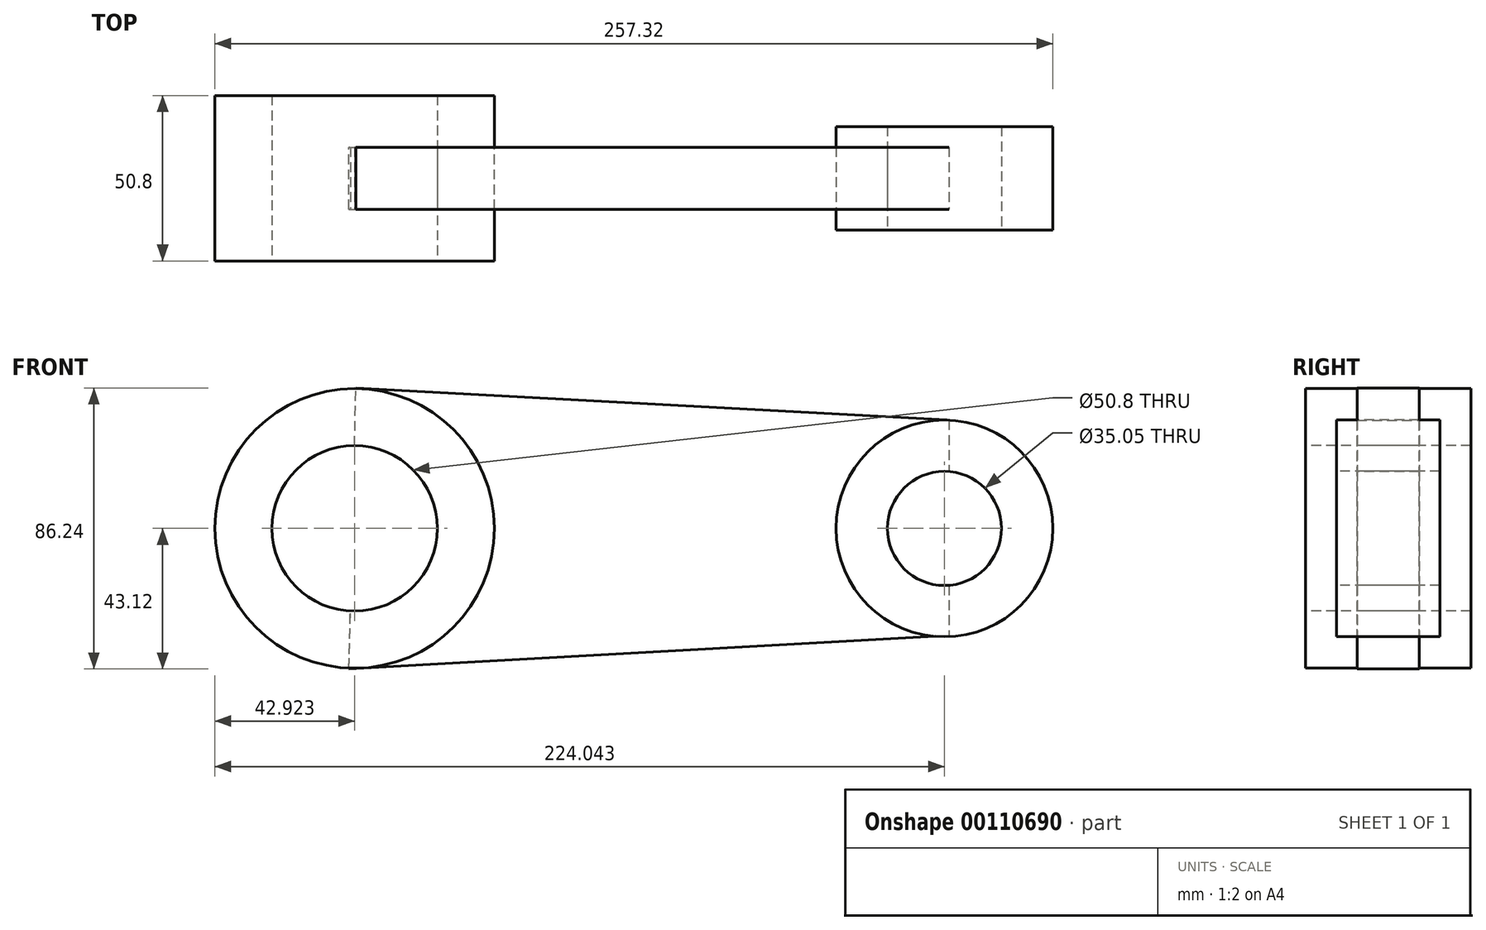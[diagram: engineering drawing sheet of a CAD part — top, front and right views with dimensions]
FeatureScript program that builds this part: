
annotation { "Feature Type Name" : "Feature", "Feature Type Description" : "" }
export const myFeature = defineFeature(function(context is Context, id is Id, definition is map)
    precondition{}
    {
        {
            var Q0;
            Q0=qCreatedBy(makeId("Front.planeOp"),FACE);
            var sketch = newSketch(context, id + "F0", { "sketchPlane" : qUnion([Q0])});
            skCircle(sketch, "E0", {"center": v(-91.09, 0) * mm, "radius": 42.93 * mm});
            skSolve(sketch);
        }
        {
            var Q0;
            Q0=qCreatedBy(makeId("Front.planeOp"),FACE);
            var sketch = newSketch(context, id + "F1", { "sketchPlane" : qUnion([Q0])});
            skCircle(sketch, "E1", {"center": v(90.03, 0) * mm, "radius": 33.27 * mm});
            skSolve(sketch);
        }
        {
            var Q0;
            Q0=makeQuery(id+"F0.imprint","IMPRINT",FACE,{"disambiguationData":[TD([[makeQuery(id+"F0.imprint","IMPRINT",EDGE,{"derivedFrom":sQuery(id+"F0.wireOp",EDGE,"E0")}),1.0]])]});
            extrude(context, id + "F2", {"entities" : qUnion([Q0]), "depth" : 25.4 * mm, "hasSecondDirection" : true, "secondDirectionOppositeDirection" : true, "secondDirectionDepth" : 25.4 * mm});
        }
        {
            var Q0;
            Q0=makeQuery(id+"F1.imprint","IMPRINT",FACE,{"disambiguationData":[TD([[makeQuery(id+"F1.imprint","IMPRINT",EDGE,{"derivedFrom":sQuery(id+"F1.wireOp",EDGE,"E1")}),1.0]])]});
            extrude(context, id + "F3", {"entities" : qUnion([Q0]), "oppositeDirection" : true, "depth" : 15.88 * mm, "hasSecondDirection" : true, "secondDirectionOppositeDirection" : false, "secondDirectionDepth" : 15.88 * mm});
        }
        {
            var Q0;
            Q0=qCreatedBy(makeId("Front.planeOp"),FACE);
            var sketch = newSketch(context, id + "F4", { "sketchPlane" : qUnion([Q0])});
            skLineSegment(sketch, "E2", {"start": v(-90.67, 43.12) * mm, "end": v(91.4, 33.23) * mm});
            skLineSegment(sketch, "E3", {"start": v(91.4, 33.23) * mm, "end": v(91.4, -32.92) * mm});
            skLineSegment(sketch, "E4", {"start": v(91.4, -32.92) * mm, "end": v(-92.84, -43.12) * mm});
            skLineSegment(sketch, "E5", {"start": v(-92.84, -43.12) * mm, "end": v(-90.67, 43.12) * mm});
            skSolve(sketch);
        }
        {
            var Q0;
            Q0=makeQuery(id+"F4.imprint","IMPRINT",FACE,{"disambiguationData":[TD([[makeQuery(id+"F4.imprint","IMPRINT",EDGE,{"derivedFrom":sQuery(id+"F4.wireOp",EDGE,"E2")}),-1.0]])]});
            extrude(context, id + "F5", {"entities" : qUnion([Q0]), "depth" : 9.52 * mm, "hasSecondDirection" : true, "secondDirectionOppositeDirection" : true, "secondDirectionDepth" : 9.52 * mm});
        }
        {
            var Q0;
            Q0=makeQuery(id+"F2.opExtrude","CAP_FACE",FACE,{"disambiguationData":[OSD([sQuery(id+"F0.wireOp",EDGE,"E0")])],"isStart":false});
            var sketch = newSketch(context, id + "F6", { "sketchPlane" : qUnion([Q0])});
            skCircle(sketch, "E6", {"center": v(-91.09, 0) * mm, "radius": 25.4 * mm});
            skSolve(sketch);
        }
        {
            var Q0;
            Q0=makeQuery(id+"F6.imprint","IMPRINT",FACE,{"disambiguationData":[TD([[makeQuery(id+"F6.imprint","IMPRINT",EDGE,{"derivedFrom":sQuery(id+"F6.wireOp",EDGE,"E6")}),1.0]])]});
            extrude(context, id + "F7", {"entities" : qUnion([Q0]), "operationType" : NewBodyOperationType.REMOVE, "oppositeDirection" : true, "depth" : 132.4 * mm});
        }
        {
            var Q0;
            Q0=makeQuery(id+"F3.opExtrude","CAP_FACE",FACE,{"disambiguationData":[OSD([sQuery(id+"F1.wireOp",EDGE,"E1")])],"isStart":true});
            var sketch = newSketch(context, id + "F8", { "sketchPlane" : qUnion([Q0])});
            skCircle(sketch, "E7", {"center": v(90.03, 0) * mm, "radius": 17.53 * mm});
            skSolve(sketch);
        }
        {
            var Q0;
            Q0=makeQuery(id+"F8.imprint","IMPRINT",FACE,{"disambiguationData":[TD([[makeQuery(id+"F8.imprint","IMPRINT",EDGE,{"derivedFrom":sQuery(id+"F8.wireOp",EDGE,"E7")}),1.0]])]});
            extrude(context, id + "F9", {"entities" : qUnion([Q0]), "operationType" : NewBodyOperationType.REMOVE, "oppositeDirection" : true, "depth" : 95.2 * mm});
        }
    });
